# Revit family: LIGHTGLASS V2 Array
name_source: partatom
category: Lighting Fixtures
units: mm (PartAtom-declared; Revit-internal decimal feet)

## family parameters
Cut with Voids When Loaded = Yes
Host = Face
Light Source = No
Part Type = Normal
Room Calculation Point = No
Round Connector Dimension = Use Diameter
Shared = No

## types (3) — shared parameters
Default Elevation = 4' - 0"
Depth from Face of Finish = 0' - 1"
Description = AREA OF UNIT CANNOT NOT EXCEED 24 SQUARE FEET
URL = WWW.LIGHTGLASSLIGHTING.COM

## per-type parameters (varying)
| type | Number of Units Along X | Number of Units Along Y | Perimeter Height | Perimeter Width | X (Mullion Count) | Y (Mullion Count) |
| LIGHTGLASS - ARRAY - 48x48 - 2x2 | 2 | 2 | 4' - 0" | 4' - 0" | 3 | 3 |
| LIGHTGLASS - ARRAY - 96x96 - 5x5 | 5 | 5 | 8' - 0" | 8' - 0" | 6 | 6 |
| LIGHTGLASS - ARRAY - 240x120 - 4x3 | 3 | 4 | 20' - 0" | 10' - 0" | 4 | 5 |

## geometry (parser evidence)
native form markers: Sweep x24
no freeform markers — native parametric forms only
